# Revit family: Clevertronics_EPIC-1500-SEN_AUB04610230001
name_source: partatom
category: Lighting Fixtures
units: mm (PartAtom-declared; Revit-internal decimal feet)

## family parameters
Cut with Voids When Loaded = No
Host = Face
Light Source = Yes
Part Type = Normal
Room Calculation Point = No
Round Connector Dimension = Use Diameter
Shared = No

## types (3) — shared parameters
Apparent Load = 0 VA
Clevertronics_Applicable Standards = AS/NZS3820, CISPR15, AS/NZS60598.1
Clevertronics_Construction = Powder Coated Sheet Metal Base, Co-extruded IP40 PC Diffuser Assembly, PC End Caps
Clevertronics_Diffuser = Co-extruded IP40 PC Diffuser Assembly
Clevertronics_Dimensions Main Enclosure = L 1533mm x W 72mm x H 78mm
Clevertronics_Driver/ Ballast = LC 57W, 700-1050mA, flexC Ip SNC4
Clevertronics_Earth Leakage = 0.152mA
Clevertronics_Emergency Driver = 1330069
Clevertronics_Height = 78 mm  [stored 0.255906 ft]
Clevertronics_IP Rating = IP20
Clevertronics_Impact Rating = IK03
Clevertronics_Inrush Current = 28.4A, <88µs
Clevertronics_Length = 1533 mm  [stored 5.02953 ft]
Clevertronics_MIC Number = AUB04610230001
Clevertronics_Material = Clevertronics_Plycarbonate Base
Clevertronics_Mounting = Surface Mount
Clevertronics_Operating Temperature = 1°C to 40°C
Clevertronics_Operating Voltage = 220-240V~ 50Hz
Clevertronics_Power Factor = 0.90 @ High Output
Clevertronics_Supply Current = 180mA +/- 20mA
Clevertronics_Weight = 2.2 Kg
Clevertronics_Width = 72 mm  [stored 0.23622 ft]
Color Filter = 16777215
Default Elevation = 1200 mm
Dimming Lamp Color Temperature Shift = <None>
Emit from Line Length = 610 mm
Lamp = Dual LED strip module, 3000K warm white, 5700K cool white, >50,000hr life, Ra>80__L70/B50 Ta 40°C; Reported >54,000hr, Projected 158,000hr__L80/B50 Ta 40°C; Reported >54,000hr, Projected 99,000hr
Manufacturer = Clevertronics
Model = EPIC-1500-SEN
Tilt Angle = -90.00°
zero-valued in all types: Clevertronics_Annotation Size

## per-type parameters (varying)
| type | Clevertronics_Power Consumption | Clevertronics_Product Description | Clevertronics_Total Lumen Output | Description | Photometric Web File |
| EPIC-1500-SEN_4000K | 45.33W | Epic 1500mm Diffused Batten, Switchable Colour & Output | 6117 lm (129.6 lm/W) | Epic 1500mm Diffused Batten, Switchable Colour | EPIC-1500-4K_IESA_G_TUV7191314725_20230817.IES |
| EPIC-1500-SEN_3000K | 47.21W | Epic 1500mm Diffused Batten, Motion Sensor,  Switchable Colour & Output | 5555 lm (117 lm/W) | Epic 1500mm Diffused Batten, Motion Sensor, Switchable Colour & Output | EPIC-1500-3K_IESA_G_TUV7191314725_20230817.IES |
| EPIC-1500-SEN_5700K | 47.49W | Epic 1500mm Diffused Batten, Switchable Colour & Output | 5883 lm (118.97 lm/W) | Epic 1500mm Diffused Batten, Switchable Colour | EPIC-1500-57K_IESA_G_TUV7191314725_20230817.IES |

note: [stored X ft] marks values corroborated as IEEE doubles in the binary element streams (Revit-internal decimal feet)

## geometry (parser evidence)
native form markers: Blend x2, Sweep x1
no freeform markers — native parametric forms only
